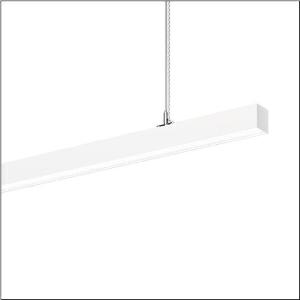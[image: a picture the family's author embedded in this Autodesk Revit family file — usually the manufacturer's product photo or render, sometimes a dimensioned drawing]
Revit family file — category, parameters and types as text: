
# Revit family: silica_r__21_51mx30da34wb_efde
name_source: partatom
category: Lighting Fixtures
units: mm (PartAtom-declared; Revit-internal decimal feet)

## family parameters
Cut with Voids When Loaded = No
Host = Face
Light Source = No
Part Type = Normal
Room Calculation Point = No
Round Connector Dimension = Use Diameter
Shared = No

## types (1)
- --- (1 x LED, 4210 lm, 27.7 W, 3000K)
    Apparent Load = 28 VA
    CIE Flux Codes = 47 79 96 57 100
    Color Rendering = 80
    Color Temperature = 3000K
    Default Elevation = 1800 mm
    Description = Silica® 21, office luminaire, primary optical cover: cover, of PMMA, opal, light emission: direct/indirect distribution, primary light characteristic: symmetric, installation type: suspended mounting, LED, rated luminous flux: 4.210lm, luminous efficacy: 152lm/W, light colour: 830, colour temperature: 3000K, with terminal, 3+2-pole, max. 2.5mm², mains connection: 220..240V, AC, 50/60Hz, rated input power: 27.7W, luminaire housing, of aluminium, traffic white (RAL 9016), length: 1.204mm, width: 53mm, height: 53mm, protection rating (complete): IP20, insulation class (complete): insulation class I (protective earthing), certification: CE, permissible operating ambient temperature: 0..+35°C, standard: EN 50419, packaging unit: 1 piece
    Height = 53 mm
    Lamp = 1 x LED
    Lamp Light Flux = 4210 lm
    Lamp Power = 27.7 W
    Lamp count = 1
    Length = 1204 mm
    Luminous efficacy = 152 lm/W
    Manufacturer = Siteco
    ModVariant = No
    Model = 51MX30DA34WB
    Mounting Place = Ceiling
    Mounting Type = Pendant
    Number of Poles = 1
    OnlyDefault = Yes
    Power Factor = 1
    Product Name = Silica® 21
    Product group = office luminaire | ceiling pendant
    ProductGroupID = 902
    Protection Class = Protection class I
    Protection Degree = IP 20
    RLX_Detail_Level = 1
    RLX_Emergency_Light_Flux = 0 lm
    RLX_Emergency_Type = 0
    RLX_Emergency_Type_DB = No
    RlxData = <blob elided: 21169 chars, md5=2fd30bcd>
    Socket = socket
    Standby Power = 0 W
    System Light Flux = 4210 lm
    System Power = 28 W
    Type Comments = factory setting: luminous flux: 100 % | dim-lin: 254 | 233 mA
    Type Image = l_1313629.jpg
    URL = http://relux.com
    VarID = @adj_065671
    Voltage = 0 V
    Weight = 0.00 kg
    Width = 53 mm

## geometry (parser evidence)
native form markers: Blend x4, Sweep x15
no freeform markers — native parametric forms only
